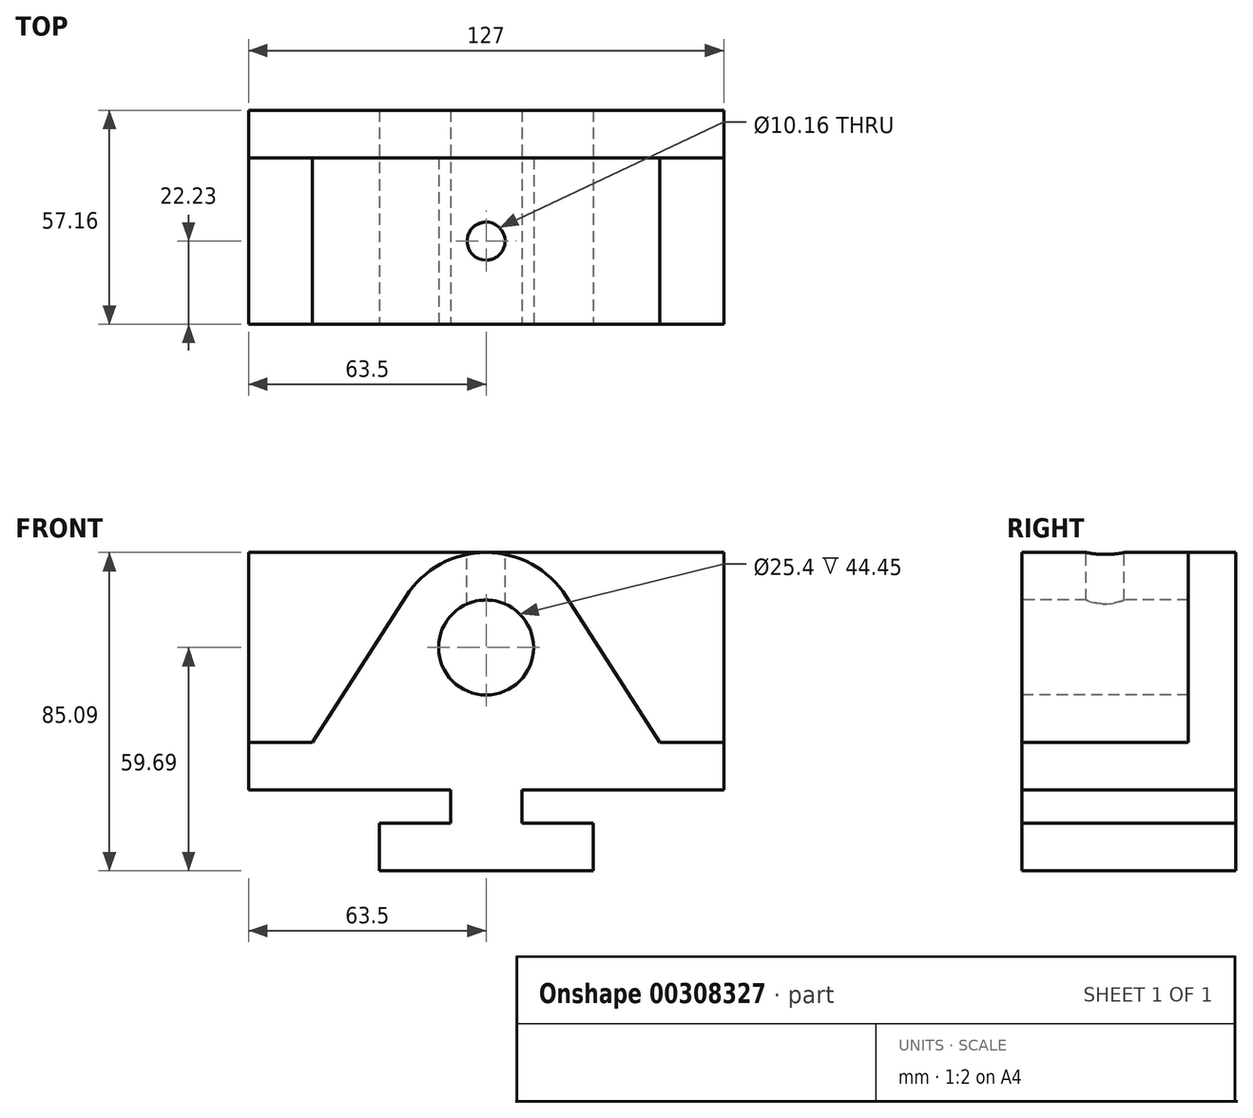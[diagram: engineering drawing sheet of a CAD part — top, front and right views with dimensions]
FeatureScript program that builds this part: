
annotation { "Feature Type Name" : "Feature", "Feature Type Description" : "" }
export const myFeature = defineFeature(function(context is Context, id is Id, definition is map)
    precondition{}
    {
        {
            var Q0;
            Q0=qCreatedBy(makeId("Front.planeOp"),FACE);
            var sketch = newSketch(context, id + "F0", { "sketchPlane" : qUnion([Q0])});
            skLineSegment(sketch, "E0", {"start": v(0, 0) * mm, "end": v(127, 0) * mm});
            skLineSegment(sketch, "E1", {"start": v(127, 0) * mm, "end": v(127, 85.09) * mm});
            skLineSegment(sketch, "E2", {"start": v(127, 85.1) * mm, "end": v(0, 85.1) * mm});
            skLineSegment(sketch, "E3", {"start": v(0, 85.09) * mm, "end": v(0, 0) * mm});
            skSolve(sketch);
        }
        {
            var Q0;
            Q0 = qSketchRegion(id + "F0", true);
            extrude(context, id + "F1", {"entities" : qUnion([Q0]), "endBound" : BoundingType.SYMMETRIC, "depth" : 57.15 * mm});
        }
        {
            var Q0;
            Q0=makeQuery(id+"F1.opExtrude","CAP_FACE",FACE,{"disambiguationData":[OSD([sQuery(id+"F0.wireOp",EDGE,"E0"),sQuery(id+"F0.wireOp",EDGE,"E1"),sQuery(id+"F0.wireOp",EDGE,"E2"),sQuery(id+"F0.wireOp",EDGE,"E3")])],"isStart":false});
            var sketch = newSketch(context, id + "F2", { "sketchPlane" : qUnion([Q0])});
            skLineSegment(sketch, "E4", {"start": v(63.5, 85.1) * mm, "end": v(63.5, -16.72) * mm, "construction": true});
            skPoint(sketch, "E4.endSnap0", {"position": v(63.5, 0) * mm});
            skLineSegment(sketch, "E5", {"start": v(34.92, 0) * mm, "end": v(34.92, 12.7) * mm});
            skLineSegment(sketch, "E6", {"start": v(34.92, 12.7) * mm, "end": v(53.97, 12.7) * mm});
            skLineSegment(sketch, "E7", {"start": v(53.97, 12.7) * mm, "end": v(53.97, 21.59) * mm});
            skLineSegment(sketch, "E8", {"start": v(0, 21.59) * mm, "end": v(53.97, 21.59) * mm});
            skLineSegment(sketch, "E9", {"start": v(0, 21.59) * mm, "end": v(0, 0) * mm});
            skLineSegment(sketch, "E10", {"start": v(0, 0) * mm, "end": v(34.92, 0) * mm});
            skLineSegment(sketch, "E11.MirrorCS", {"start": v(92.08, 0) * mm, "end": v(92.08, 12.7) * mm});
            skLineSegment(sketch, "E12.MirrorCS", {"start": v(92.08, 12.7) * mm, "end": v(73.03, 12.7) * mm});
            skLineSegment(sketch, "E13.MirrorCS", {"start": v(73.03, 12.7) * mm, "end": v(73.03, 21.59) * mm});
            skLineSegment(sketch, "E14.MirrorCS", {"start": v(127, 21.59) * mm, "end": v(73.03, 21.59) * mm});
            skLineSegment(sketch, "E15.MirrorCS", {"start": v(127, 21.59) * mm, "end": v(127, 0) * mm});
            skLineSegment(sketch, "E16.MirrorCS", {"start": v(127, 0) * mm, "end": v(92.07, 0) * mm});
            skSolve(sketch);
        }
        {
            var Q0;
            Q0 = qSketchRegion(id + "F2", true);
            extrude(context, id + "F3", {"entities" : qUnion([Q0]), "operationType" : NewBodyOperationType.REMOVE, "endBound" : BoundingType.THROUGH_ALL, "oppositeDirection" : true, "depth" : 25.4 * mm});
        }
        {
            var Q0;
            Q0=makeQuery(id+"F1.opExtrude","CAP_FACE",FACE,{"disambiguationData":[OSD([sQuery(id+"F0.wireOp",EDGE,"E0"),sQuery(id+"F0.wireOp",EDGE,"E1"),sQuery(id+"F0.wireOp",EDGE,"E2"),sQuery(id+"F0.wireOp",EDGE,"E3")])],"isStart":false});
            var sketch = newSketch(context, id + "F4", { "sketchPlane" : qUnion([Q0])});
            skLineSegment(sketch, "E17", {"start": v(0, 34.3) * mm, "end": v(17.15, 34.3) * mm});
            skLineSegment(sketch, "E18", {"start": v(63.5, 85.1) * mm, "end": v(63.5, -14.94) * mm, "construction": true});
            skPoint(sketch, "E18.endSnap0", {"position": v(63.5, 0) * mm});
            skLineSegment(sketch, "E19", {"start": v(17.14, 34.29) * mm, "end": v(42.1, 73.36) * mm});
            skArc(sketch, "E20", {"start": v(42.1, 73.36) * mm, "mid": v(51.3, 81.97) * mm, "end": v(63.5, 85.1) * mm});
            skCircle(sketch, "E21", {"center": v(63.5, 59.7) * mm, "radius": 12.7 * mm});
            skLineSegment(sketch, "E22.MirrorCS", {"start": v(127, 34.3) * mm, "end": v(109.85, 34.3) * mm});
            skLineSegment(sketch, "E23.MirrorCS", {"start": v(109.86, 34.3) * mm, "end": v(84.9, 73.36) * mm});
            skArc(sketch, "E24.MirrorCS", {"start": v(84.9, 73.36) * mm, "mid": v(75.7, 81.97) * mm, "end": v(63.5, 85.1) * mm});
            skSolve(sketch);
        }
        {
            var Q0;
            Q0=makeQuery(id+"F1.opExtrude","SWEPT_FACE",FACE,{"disambiguationData":[OSD([sQuery(id+"F0.wireOp",EDGE,"E2")])]});
            var sketch = newSketch(context, id + "F5", { "sketchPlane" : qUnion([Q0])});
            skCircle(sketch, "E25", {"center": v(63.5, -6.35) * mm, "radius": 5.08 * mm});
            skPoint(sketch, "E25.centerSnap0", {"position": v(63.5, 28.58) * mm});
            skSolve(sketch);
        }
        {
            var Q0;
            Q0 = qSketchRegion(id + "F5", true);
            extrude(context, id + "F6", {"entities" : qUnion([Q0]), "operationType" : NewBodyOperationType.REMOVE, "oppositeDirection" : true, "depth" : 25.4 * mm});
        }
        {
            var Q0;
            Q0 = qSketchRegion(id + "F4", true);
            var Q1;
            {var subQ4=sQuery(id+"F4.wireOp",EDGE,"E17");Q1=makeQuery(id+"F4.imprint","IMPRINT",FACE,{"disambiguationData":[TD([[makeQuery(id+"F4.imprint","IMPRINT",EDGE,{"derivedFrom":subQ4}),1.0]])]});}
            var Q2;
            {var subQ4=sQuery(id+"F4.wireOp",EDGE,"E22.MirrorCS");Q2=makeQuery(id+"F4.imprint","IMPRINT",FACE,{"disambiguationData":[TD([[makeQuery(id+"F4.imprint","IMPRINT",EDGE,{"derivedFrom":subQ4}),-1.0]])]});}
            extrude(context, id + "F7", {"entities" : qUnion([Q0, Q1, Q2]), "operationType" : NewBodyOperationType.REMOVE, "oppositeDirection" : true, "depth" : 44.45 * mm});
        }
    });
